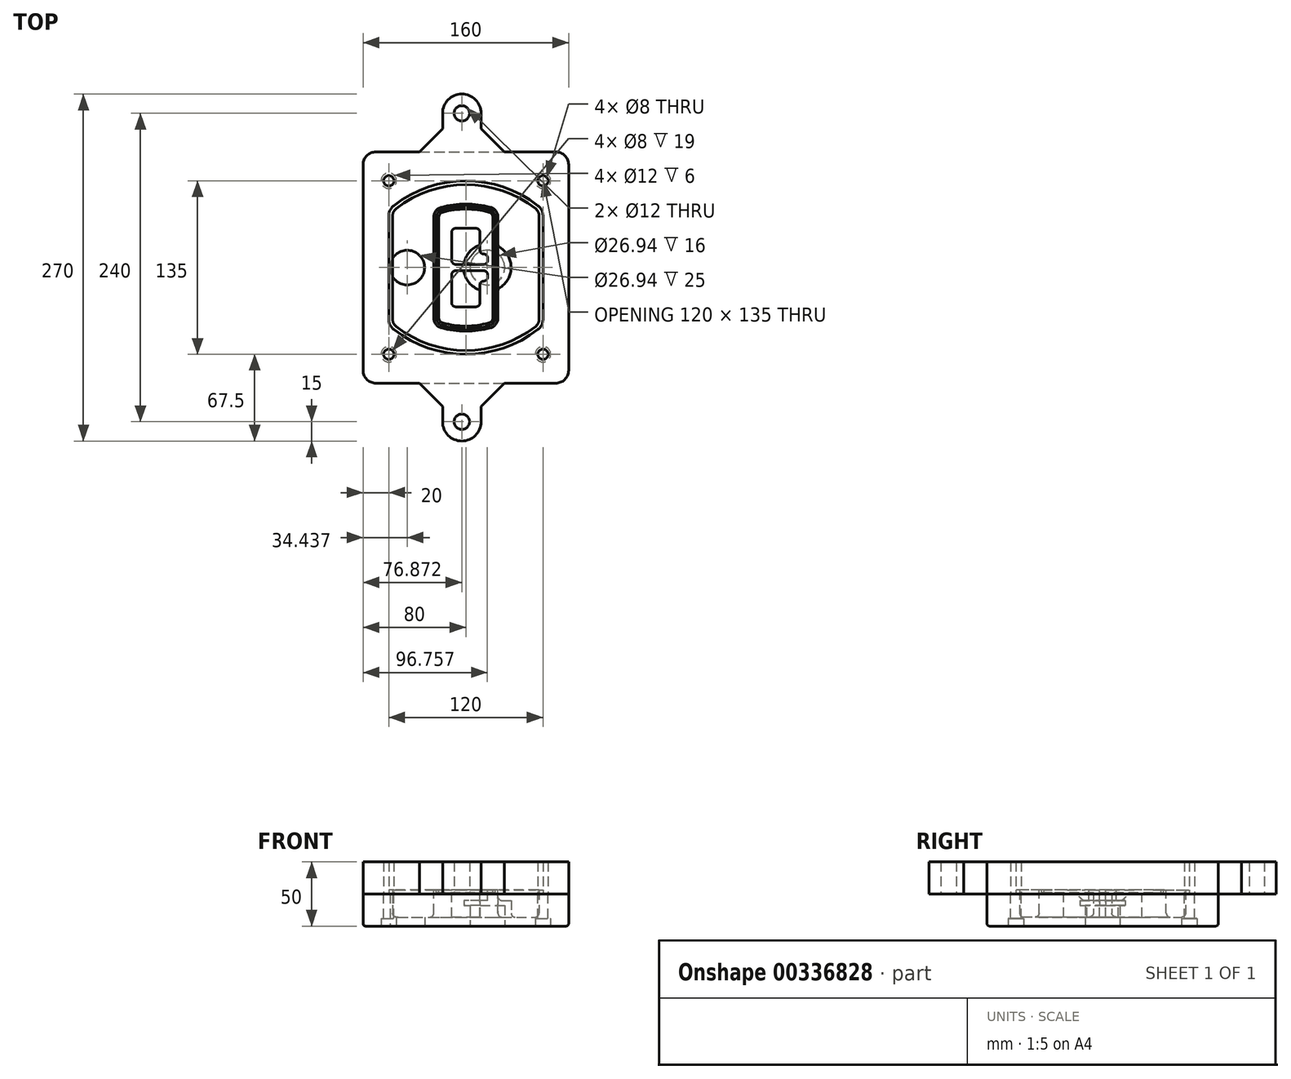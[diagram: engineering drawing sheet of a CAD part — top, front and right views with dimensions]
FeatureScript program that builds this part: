
annotation { "Feature Type Name" : "Feature", "Feature Type Description" : "" }
export const myFeature = defineFeature(function(context is Context, id is Id, definition is map)
    precondition{}
    {
        {
            var Q0;
            Q0=qCreatedBy(makeId("Top.planeOp"),FACE);
            var sketch = newSketch(context, id + "F0", { "sketchPlane" : qUnion([Q0])});
            skPoint(sketch, "E0.rect.middle", {"position": v(0, 0) * mm});
            skLineSegment(sketch, "E1.bottom", {"start": v(-70, -90) * mm, "end": v(70, -90) * mm});
            skLineSegment(sketch, "E1.top", {"start": v(-70, 90) * mm, "end": v(70, 90) * mm});
            skLineSegment(sketch, "E1.left", {"start": v(-80, -80) * mm, "end": v(-80, 80) * mm});
            skLineSegment(sketch, "E1.right", {"start": v(80, -80) * mm, "end": v(80, 80) * mm});
            skLineSegment(sketch, "E2", {"start": v(-80, 90) * mm, "end": v(80, -90) * mm, "construction": true});
            skLineSegment(sketch, "E3", {"start": v(80, 90) * mm, "end": v(-80, -90) * mm, "construction": true});
            skCircle(sketch, "E4", {"center": v(-60, 67.5) * mm, "radius": 4 * mm});
            skCircle(sketch, "E5", {"center": v(60, 67.5) * mm, "radius": 4 * mm});
            skCircle(sketch, "E6", {"center": v(60, -67.5) * mm, "radius": 4 * mm});
            skCircle(sketch, "E7", {"center": v(-60, -67.5) * mm, "radius": 4 * mm});
            skLineSegment(sketch, "E8", {"start": v(-60, 67.5) * mm, "end": v(60, 67.5) * mm, "construction": true});
            skLineSegment(sketch, "E9", {"start": v(60, 67.5) * mm, "end": v(60, -67.5) * mm, "construction": true});
            skLineSegment(sketch, "E10", {"start": v(60, -67.5) * mm, "end": v(-60, -67.5) * mm, "construction": true});
            skLineSegment(sketch, "E11", {"start": v(-60, -67.5) * mm, "end": v(-60, 67.5) * mm, "construction": true});
            skLineSegment(sketch, "E12", {"start": v(-60, 40.3) * mm, "end": v(-60, -40.3) * mm});
            skLineSegment(sketch, "E13", {"start": v(60, 40.3) * mm, "end": v(60, -40.3) * mm});
            skArc(sketch, "E14", {"start": v(56.15, 48.18) * mm, "mid": v(0, 67.5) * mm, "end": v(-56.15, 48.18) * mm});
            skArc(sketch, "E15", {"start": v(-56.15, -48.18) * mm, "mid": v(0, -67.5) * mm, "end": v(56.15, -48.18) * mm});
            skLineSegment(sketch, "E16", {"start": v(-60, 0) * mm, "end": v(60, 0) * mm, "construction": true});
            skPoint(sketch, "E17.visualSharp", {"position": v(-60, -45) * mm});
            skArc(sketch, "E17.filletArc", {"start": v(-60, -40.3) * mm, "mid": v(-58.99, -44.68) * mm, "end": v(-56.15, -48.18) * mm});
            skPoint(sketch, "E18.visualSharp", {"position": v(-60, 45) * mm});
            skArc(sketch, "E18.filletArc", {"start": v(-56.15, 48.18) * mm, "mid": v(-58.99, 44.68) * mm, "end": v(-60, 40.3) * mm});
            skPoint(sketch, "E19.visualSharp", {"position": v(60, 45) * mm});
            skArc(sketch, "E19.filletArc", {"start": v(60, 40.3) * mm, "mid": v(58.99, 44.68) * mm, "end": v(56.15, 48.18) * mm});
            skPoint(sketch, "E20.visualSharp", {"position": v(60, -45) * mm});
            skArc(sketch, "E20.filletArc", {"start": v(56.15, -48.18) * mm, "mid": v(58.99, -44.68) * mm, "end": v(60, -40.3) * mm});
            skPoint(sketch, "E21.visualSharp", {"position": v(-80, 90) * mm});
            skArc(sketch, "E21.filletArc", {"start": v(-70, 90) * mm, "mid": v(-77.07, 87.07) * mm, "end": v(-80, 80) * mm});
            skPoint(sketch, "E22.visualSharp", {"position": v(80, 90) * mm});
            skArc(sketch, "E22.filletArc", {"start": v(80, 80) * mm, "mid": v(77.07, 87.07) * mm, "end": v(70, 90) * mm});
            skPoint(sketch, "E23.visualSharp", {"position": v(80, -90) * mm});
            skArc(sketch, "E23.filletArc", {"start": v(70, -90) * mm, "mid": v(77.07, -87.07) * mm, "end": v(80, -80) * mm});
            skPoint(sketch, "E24.visualSharp", {"position": v(-80, -90) * mm});
            skArc(sketch, "E24.filletArc", {"start": v(-80, -80) * mm, "mid": v(-77.07, -87.07) * mm, "end": v(-70, -90) * mm});
            skArc(sketch, "E25.0", {"start": v(57, 40.3) * mm, "mid": v(56.3, 43.36) * mm, "end": v(54.3, 45.81) * mm});
            skLineSegment(sketch, "E25.1", {"start": v(57, 40.3) * mm, "end": v(57, -40.3) * mm});
            skArc(sketch, "E25.2", {"start": v(54.3, -45.81) * mm, "mid": v(56.3, -43.36) * mm, "end": v(57, -40.3) * mm});
            skArc(sketch, "E25.3", {"start": v(-54.3, -45.81) * mm, "mid": v(0, -64.5) * mm, "end": v(54.3, -45.81) * mm});
            skArc(sketch, "E25.4", {"start": v(-57, -40.3) * mm, "mid": v(-56.3, -43.36) * mm, "end": v(-54.3, -45.81) * mm});
            skArc(sketch, "E25.5", {"start": v(54.3, 45.81) * mm, "mid": v(0, 64.5) * mm, "end": v(-54.3, 45.81) * mm});
            skLineSegment(sketch, "E25.6", {"start": v(-57, 40.3) * mm, "end": v(-57, -40.3) * mm});
            skArc(sketch, "E25.7", {"start": v(-54.3, 45.81) * mm, "mid": v(-56.3, 43.36) * mm, "end": v(-57, 40.3) * mm});
            skArc(sketch, "E26.0", {"start": v(-58.62, 51.33) * mm, "mid": v(-62.58, 46.43) * mm, "end": v(-64, 40.3) * mm});
            skArc(sketch, "E26.1", {"start": v(58.62, 51.33) * mm, "mid": v(0, 71.5) * mm, "end": v(-58.62, 51.33) * mm});
            skArc(sketch, "E26.2", {"start": v(64, 40.3) * mm, "mid": v(62.58, 46.43) * mm, "end": v(58.62, 51.33) * mm});
            skLineSegment(sketch, "E26.3", {"start": v(64, 40.3) * mm, "end": v(64, -40.3) * mm});
            skArc(sketch, "E26.4", {"start": v(58.62, -51.33) * mm, "mid": v(62.58, -46.43) * mm, "end": v(64, -40.3) * mm});
            skLineSegment(sketch, "E26.5", {"start": v(-64, 40.3) * mm, "end": v(-64, -40.3) * mm});
            skArc(sketch, "E26.6", {"start": v(-58.62, -51.33) * mm, "mid": v(0, -71.5) * mm, "end": v(58.62, -51.33) * mm});
            skArc(sketch, "E26.7", {"start": v(-64, -40.3) * mm, "mid": v(-62.58, -46.43) * mm, "end": v(-58.62, -51.33) * mm});
            skSolve(sketch);
        }
        {
            var Q0;
            Q0=makeQuery(id+"F0.imprint","IMPRINT",FACE,{"disambiguationData":[TD([[makeQuery(id+"F0.imprint","IMPRINT",EDGE,{"derivedFrom":sQuery(id+"F0.wireOp",EDGE,"E1.bottom")}),1.0]])]});
            var Q1;
            Q1=makeQuery(id+"F0.imprint","IMPRINT",FACE,{"disambiguationData":[TD([[makeQuery(id+"F0.imprint","IMPRINT",EDGE,{"derivedFrom":sQuery(id+"F0.wireOp",EDGE,"E12")}),1.0]])]});
            var Q2;
            Q2=makeQuery(id+"F0.imprint","IMPRINT",FACE,{"disambiguationData":[TD([[makeQuery(id+"F0.imprint","IMPRINT",EDGE,{"derivedFrom":sQuery(id+"F0.wireOp",EDGE,"E25.0")}),1.0]])]});
            var Q3;
            Q3=makeQuery(id+"F0.imprint","IMPRINT",FACE,{"disambiguationData":[TD([[makeQuery(id+"F0.imprint","IMPRINT",EDGE,{"derivedFrom":sQuery(id+"F0.wireOp",EDGE,"E12")}),-1.0]])]});
            extrude(context, id + "F1", {"entities" : qUnion([Q0, Q1, Q2, Q3]), "oppositeDirection" : true, "depth" : 25 * mm});
        }
        {
            var Q0;
            Q0=makeQuery(id+"F0.imprint","IMPRINT",FACE,{"disambiguationData":[TD([[makeQuery(id+"F0.imprint","IMPRINT",EDGE,{"derivedFrom":sQuery(id+"F0.wireOp",EDGE,"E12")}),1.0]])]});
            extrude(context, id + "F2", {"entities" : qUnion([Q0]), "operationType" : NewBodyOperationType.ADD, "depth" : 3 * mm});
        }
        {
            var Q0;
            Q0=makeQuery(id+"F0.imprint","IMPRINT",FACE,{"disambiguationData":[TD([[makeQuery(id+"F0.imprint","IMPRINT",EDGE,{"derivedFrom":sQuery(id+"F0.wireOp",EDGE,"E25.0")}),1.0]])]});
            extrude(context, id + "F3", {"entities" : qUnion([Q0]), "operationType" : NewBodyOperationType.REMOVE, "oppositeDirection" : true, "depth" : 18 * mm});
        }
        {
            var Q0;
            Q0=makeQuery(id+"F2.opExtrude","CAP_FACE",FACE,{"disambiguationData":[OSD([sQuery(id+"F0.wireOp",EDGE,"E12"),sQuery(id+"F0.wireOp",EDGE,"E13"),sQuery(id+"F0.wireOp",EDGE,"E14"),sQuery(id+"F0.wireOp",EDGE,"E15"),sQuery(id+"F0.wireOp",EDGE,"E17.filletArc"),sQuery(id+"F0.wireOp",EDGE,"E18.filletArc"),sQuery(id+"F0.wireOp",EDGE,"E19.filletArc"),sQuery(id+"F0.wireOp",EDGE,"E20.filletArc"),sQuery(id+"F0.wireOp",EDGE,"E25.0"),sQuery(id+"F0.wireOp",EDGE,"E25.1"),sQuery(id+"F0.wireOp",EDGE,"E25.2"),sQuery(id+"F0.wireOp",EDGE,"E25.3"),sQuery(id+"F0.wireOp",EDGE,"E25.4"),sQuery(id+"F0.wireOp",EDGE,"E25.5"),sQuery(id+"F0.wireOp",EDGE,"E25.6"),sQuery(id+"F0.wireOp",EDGE,"E25.7")])],"isStart":false});
            var sketch = newSketch(context, id + "F4", { "sketchPlane" : qUnion([Q0])});
            skArc(sketch, "E27.0", {"start": v(-19.08, -46.97) * mm, "mid": v(0, -49.5) * mm, "end": v(19.08, -46.97) * mm});
            skArc(sketch, "E28.0", {"start": v(19.08, 46.97) * mm, "mid": v(0, 49.5) * mm, "end": v(-19.08, 46.97) * mm});
            skLineSegment(sketch, "E29", {"start": v(-25, 39.25) * mm, "end": v(-25, -39.25) * mm});
            skLineSegment(sketch, "E30", {"start": v(25, 39.25) * mm, "end": v(25, -39.25) * mm});
            skLineSegment(sketch, "E31", {"start": v(-25, 45.1) * mm, "end": v(25, 45.1) * mm, "construction": true});
            skLineSegment(sketch, "E32", {"start": v(-25, -45.1) * mm, "end": v(25, -45.1) * mm, "construction": true});
            skPoint(sketch, "E33.visualSharp", {"position": v(-25, 45.1) * mm});
            skArc(sketch, "E33.filletArc", {"start": v(-19.08, 46.97) * mm, "mid": v(-23.35, 44.11) * mm, "end": v(-25, 39.25) * mm});
            skPoint(sketch, "E34.visualSharp", {"position": v(25, 45.1) * mm});
            skArc(sketch, "E34.filletArc", {"start": v(25, 39.25) * mm, "mid": v(23.35, 44.11) * mm, "end": v(19.08, 46.97) * mm});
            skPoint(sketch, "E35.visualSharp", {"position": v(25, -45.1) * mm});
            skArc(sketch, "E35.filletArc", {"start": v(19.08, -46.97) * mm, "mid": v(23.35, -44.11) * mm, "end": v(25, -39.25) * mm});
            skPoint(sketch, "E36.visualSharp", {"position": v(-25, -45.1) * mm});
            skArc(sketch, "E36.filletArc", {"start": v(-25, -39.25) * mm, "mid": v(-23.35, -44.11) * mm, "end": v(-19.08, -46.97) * mm});
            skArc(sketch, "E37.0", {"start": v(54.3, 45.81) * mm, "mid": v(0, 64.5) * mm, "end": v(-54.3, 45.81) * mm});
            skArc(sketch, "E37.1", {"start": v(-54.3, 45.81) * mm, "mid": v(-56.3, 43.36) * mm, "end": v(-57, 40.3) * mm});
            skLineSegment(sketch, "E37.2", {"start": v(-57, 40.3) * mm, "end": v(-57, -40.3) * mm});
            skArc(sketch, "E37.3", {"start": v(-57, -40.3) * mm, "mid": v(-56.3, -43.36) * mm, "end": v(-54.3, -45.81) * mm});
            skArc(sketch, "E37.4", {"start": v(-54.3, -45.81) * mm, "mid": v(0, -64.5) * mm, "end": v(54.3, -45.81) * mm});
            skArc(sketch, "E37.5", {"start": v(54.3, -45.81) * mm, "mid": v(56.3, -43.36) * mm, "end": v(57, -40.3) * mm});
            skLineSegment(sketch, "E37.6", {"start": v(57, 40.3) * mm, "end": v(57, -40.3) * mm});
            skArc(sketch, "E37.7", {"start": v(57, 40.3) * mm, "mid": v(56.3, 43.36) * mm, "end": v(54.3, 45.81) * mm});
            skLineSegment(sketch, "E38.0", {"start": v(23, 39.25) * mm, "end": v(23, -39.25) * mm});
            skArc(sketch, "E38.1", {"start": v(18.56, -45.04) * mm, "mid": v(21.76, -42.9) * mm, "end": v(23, -39.25) * mm});
            skArc(sketch, "E38.2", {"start": v(-18.56, -45.04) * mm, "mid": v(0, -47.5) * mm, "end": v(18.56, -45.04) * mm});
            skArc(sketch, "E38.3", {"start": v(-23, -39.25) * mm, "mid": v(-21.76, -42.9) * mm, "end": v(-18.56, -45.04) * mm});
            skLineSegment(sketch, "E38.4", {"start": v(-23, 39.25) * mm, "end": v(-23, -39.25) * mm});
            skArc(sketch, "E38.5", {"start": v(23, 39.25) * mm, "mid": v(21.76, 42.9) * mm, "end": v(18.56, 45.04) * mm});
            skArc(sketch, "E38.6", {"start": v(-18.56, 45.04) * mm, "mid": v(-21.76, 42.9) * mm, "end": v(-23, 39.25) * mm});
            skArc(sketch, "E38.7", {"start": v(18.56, 45.04) * mm, "mid": v(0, 47.5) * mm, "end": v(-18.56, 45.04) * mm});
            skArc(sketch, "E39.0", {"start": v(21, 39.25) * mm, "mid": v(20.18, 41.68) * mm, "end": v(18.04, 43.1) * mm});
            skLineSegment(sketch, "E39.1", {"start": v(21, 39.25) * mm, "end": v(21, -39.25) * mm});
            skArc(sketch, "E39.2", {"start": v(18.04, -43.1) * mm, "mid": v(20.18, -41.68) * mm, "end": v(21, -39.25) * mm});
            skArc(sketch, "E39.3", {"start": v(-18.04, -43.1) * mm, "mid": v(0, -45.5) * mm, "end": v(18.04, -43.1) * mm});
            skArc(sketch, "E39.4", {"start": v(-21, -39.25) * mm, "mid": v(-20.18, -41.68) * mm, "end": v(-18.04, -43.1) * mm});
            skArc(sketch, "E39.5", {"start": v(18.04, 43.1) * mm, "mid": v(0, 45.5) * mm, "end": v(-18.04, 43.1) * mm});
            skLineSegment(sketch, "E39.6", {"start": v(-21, 39.25) * mm, "end": v(-21, -39.25) * mm});
            skArc(sketch, "E39.7", {"start": v(-18.04, 43.1) * mm, "mid": v(-20.18, 41.68) * mm, "end": v(-21, 39.25) * mm});
            skLineSegment(sketch, "E40", {"start": v(-25, 0) * mm, "end": v(25, 0) * mm, "construction": true});
            skLineSegment(sketch, "E41", {"start": v(-11, 5.5) * mm, "end": v(-11, 27.5) * mm});
            skLineSegment(sketch, "E42", {"start": v(-8, 30.5) * mm, "end": v(8, 30.5) * mm});
            skLineSegment(sketch, "E43", {"start": v(11, 27.5) * mm, "end": v(11, 13.5) * mm});
            skLineSegment(sketch, "E44", {"start": v(14, 10.5) * mm, "end": v(14, 10.5) * mm});
            skLineSegment(sketch, "E45", {"start": v(17, 7.5) * mm, "end": v(17, 5.5) * mm});
            skLineSegment(sketch, "E46", {"start": v(14, 2.5) * mm, "end": v(-8, 2.5) * mm});
            skPoint(sketch, "E47.visualSharp", {"position": v(-11, 30.5) * mm});
            skArc(sketch, "E47.filletArc", {"start": v(-8, 30.5) * mm, "mid": v(-10.12, 29.62) * mm, "end": v(-11, 27.5) * mm});
            skPoint(sketch, "E48.visualSharp", {"position": v(11, 30.5) * mm});
            skArc(sketch, "E48.filletArc", {"start": v(11, 27.5) * mm, "mid": v(10.12, 29.62) * mm, "end": v(8, 30.5) * mm});
            skPoint(sketch, "E49.visualSharp", {"position": v(11, 10.5) * mm});
            skArc(sketch, "E49.filletArc", {"start": v(11, 13.5) * mm, "mid": v(11.88, 11.38) * mm, "end": v(14, 10.5) * mm});
            skPoint(sketch, "E50.visualSharp", {"position": v(17, 10.5) * mm});
            skArc(sketch, "E50.filletArc", {"start": v(17, 7.5) * mm, "mid": v(16.12, 9.62) * mm, "end": v(14, 10.5) * mm});
            skPoint(sketch, "E51.visualSharp", {"position": v(17, 2.5) * mm});
            skArc(sketch, "E51.filletArc", {"start": v(14, 2.5) * mm, "mid": v(16.12, 3.38) * mm, "end": v(17, 5.5) * mm});
            skPoint(sketch, "E52.visualSharp", {"position": v(-11, 2.5) * mm});
            skArc(sketch, "E52.filletArc", {"start": v(-11, 5.5) * mm, "mid": v(-10.12, 3.38) * mm, "end": v(-8, 2.5) * mm});
            skLineSegment(sketch, "E53.0.MirrorCS", {"start": v(14, -2.5) * mm, "end": v(-8, -2.5) * mm});
            skArc(sketch, "E54.0.MirrorCS", {"start": v(-11, -5.5) * mm, "mid": v(-10.12, -3.38) * mm, "end": v(-8, -2.5) * mm});
            skLineSegment(sketch, "E55.0.MirrorCS", {"start": v(-11, -5.5) * mm, "end": v(-11, -27.5) * mm});
            skArc(sketch, "E56.0.MirrorCS", {"start": v(-8, -30.5) * mm, "mid": v(-10.12, -29.62) * mm, "end": v(-11, -27.5) * mm});
            skLineSegment(sketch, "E57.0.MirrorCS", {"start": v(-8, -30.5) * mm, "end": v(8, -30.5) * mm});
            skArc(sketch, "E58.0.MirrorCS", {"start": v(11, -27.5) * mm, "mid": v(10.12, -29.62) * mm, "end": v(8, -30.5) * mm});
            skLineSegment(sketch, "E59.0.MirrorCS", {"start": v(11, -27.5) * mm, "end": v(11, -13.5) * mm});
            skArc(sketch, "E60.0.MirrorCS", {"start": v(11, -13.5) * mm, "mid": v(11.88, -11.38) * mm, "end": v(14, -10.5) * mm});
            skArc(sketch, "E61.0.MirrorCS", {"start": v(17, -7.5) * mm, "mid": v(16.12, -9.62) * mm, "end": v(14, -10.5) * mm});
            skLineSegment(sketch, "E62.0.MirrorCS", {"start": v(17, -7.5) * mm, "end": v(17, -5.5) * mm});
            skArc(sketch, "E63.0.MirrorCS", {"start": v(14, -2.5) * mm, "mid": v(16.12, -3.38) * mm, "end": v(17, -5.5) * mm});
            skSolve(sketch);
        }
        {
            var Q0;
            Q0=makeQuery(id+"F4.imprint","IMPRINT",FACE,{"disambiguationData":[TD([[makeQuery(id+"F4.imprint","IMPRINT",EDGE,{"derivedFrom":sQuery(id+"F4.wireOp",EDGE,"E27.0")}),1.0]])]});
            var Q1;
            Q1=makeQuery(id+"F4.imprint","IMPRINT",FACE,{"disambiguationData":[TD([[makeQuery(id+"F4.imprint","IMPRINT",EDGE,{"derivedFrom":sQuery(id+"F4.wireOp",EDGE,"E38.0")}),-1.0]])]});
            var Q2;
            Q2=makeQuery(id+"F4.imprint","IMPRINT",FACE,{"disambiguationData":[TD([[makeQuery(id+"F4.imprint","IMPRINT",EDGE,{"derivedFrom":sQuery(id+"F4.wireOp",EDGE,"E39.0")}),1.0]])]});
            extrude(context, id + "F5", {"entities" : qUnion([Q0, Q1, Q2]), "operationType" : NewBodyOperationType.ADD, "endBound" : BoundingType.UP_TO_NEXT, "oppositeDirection" : true, "depth" : 25 * mm});
        }
        {
            var Q0;
            Q0=makeQuery(id+"F4.imprint","IMPRINT",FACE,{"disambiguationData":[TD([[makeQuery(id+"F4.imprint","IMPRINT",EDGE,{"derivedFrom":sQuery(id+"F4.wireOp",EDGE,"E38.0")}),-1.0]])]});
            extrude(context, id + "F6", {"entities" : qUnion([Q0]), "operationType" : NewBodyOperationType.REMOVE, "oppositeDirection" : true, "depth" : 2 * mm});
        }
        {
            var Q0;
            Q0=makeQuery(id+"F1.opExtrude","CAP_FACE",FACE,{"disambiguationData":[OSD([sQuery(id+"F0.wireOp",EDGE,"E1.bottom"),sQuery(id+"F0.wireOp",EDGE,"E1.top"),sQuery(id+"F0.wireOp",EDGE,"E1.left"),sQuery(id+"F0.wireOp",EDGE,"E1.right"),sQuery(id+"F0.wireOp",EDGE,"E4"),sQuery(id+"F0.wireOp",EDGE,"E5"),sQuery(id+"F0.wireOp",EDGE,"E6"),sQuery(id+"F0.wireOp",EDGE,"E7"),sQuery(id+"F0.wireOp",EDGE,"E21.filletArc"),sQuery(id+"F0.wireOp",EDGE,"E22.filletArc"),sQuery(id+"F0.wireOp",EDGE,"E23.filletArc"),sQuery(id+"F0.wireOp",EDGE,"E24.filletArc")])],"isStart":false});
            var sketch = newSketch(context, id + "F7", { "sketchPlane" : qUnion([Q0])});
            skCircle(sketch, "E64", {"center": v(16.76, 0) * mm, "radius": 13.47 * mm});
            skCircle(sketch, "E65", {"center": v(-45.56, 0) * mm, "radius": 13.47 * mm});
            skLineSegment(sketch, "E66", {"start": v(80, 0) * mm, "end": v(-80, 0) * mm});
            skCircle(sketch, "E67", {"center": v(16.76, 0) * mm, "radius": 18.47 * mm});
            skCircle(sketch, "E68", {"center": v(60, -67.5) * mm, "radius": 6 * mm});
            skCircle(sketch, "E69", {"center": v(-60, -67.5) * mm, "radius": 6 * mm});
            skCircle(sketch, "E70", {"center": v(-60, 67.5) * mm, "radius": 6 * mm});
            skCircle(sketch, "E71", {"center": v(60, 67.5) * mm, "radius": 6 * mm});
            skSolve(sketch);
        }
        {
            var Q0;
            {var subQ1=sQuery(id+"F7.wireOp",EDGE,"E66");var subQ4=sQuery(id+"F7.wireOp",EDGE,"E64");var subQ6=makeQuery(id+"F7.imprint","INTERSECT",VERTEX,{"disambiguationData":[OD(0.0)],"derivedFrom":[subQ4,subQ1]});Q0=makeQuery(id+"F7.imprint","IMPRINT",FACE,{"disambiguationData":[TD([[makeQuery(id+"F7.imprint","IMPRINT",EDGE,{"disambiguationData":[TD([[subQ6,-1.0]])],"derivedFrom":subQ4}),-1.0]])]});}
            var Q1;
            {var subQ0=sQuery(id+"F7.wireOp",EDGE,"E66");var subQ1=sQuery(id+"F7.wireOp",EDGE,"E64");var subQ3=makeQuery(id+"F7.imprint","INTERSECT",VERTEX,{"disambiguationData":[OD(0.0)],"derivedFrom":[subQ1,subQ0]});Q1=makeQuery(id+"F7.imprint","IMPRINT",FACE,{"disambiguationData":[TD([[makeQuery(id+"F7.imprint","IMPRINT",EDGE,{"disambiguationData":[TD([[subQ3,-1.0]])],"derivedFrom":subQ1}),1.0]])]});}
            var Q2;
            {var subQ0=sQuery(id+"F7.wireOp",EDGE,"E66");var subQ1=sQuery(id+"F7.wireOp",EDGE,"E64");var subQ3=makeQuery(id+"F7.imprint","INTERSECT",VERTEX,{"disambiguationData":[OD(0.0)],"derivedFrom":[subQ1,subQ0]});Q2=makeQuery(id+"F7.imprint","IMPRINT",FACE,{"disambiguationData":[TD([[makeQuery(id+"F7.imprint","IMPRINT",EDGE,{"disambiguationData":[TD([[subQ3,1.0]])],"derivedFrom":subQ1}),1.0]])]});}
            var Q3;
            {var subQ1=sQuery(id+"F7.wireOp",EDGE,"E66");var subQ4=sQuery(id+"F7.wireOp",EDGE,"E64");var subQ6=makeQuery(id+"F7.imprint","INTERSECT",VERTEX,{"disambiguationData":[OD(0.0)],"derivedFrom":[subQ4,subQ1]});Q3=makeQuery(id+"F7.imprint","IMPRINT",FACE,{"disambiguationData":[TD([[makeQuery(id+"F7.imprint","IMPRINT",EDGE,{"disambiguationData":[TD([[subQ6,1.0]])],"derivedFrom":subQ4}),-1.0]])]});}
            extrude(context, id + "F8", {"entities" : qUnion([Q0, Q1, Q2, Q3]), "operationType" : NewBodyOperationType.ADD, "oppositeDirection" : true, "depth" : 20 * mm});
        }
        {
            var Q0;
            {var subQ0=sQuery(id+"F7.wireOp",EDGE,"E66");var subQ1=sQuery(id+"F7.wireOp",EDGE,"E64");var subQ3=makeQuery(id+"F7.imprint","INTERSECT",VERTEX,{"disambiguationData":[OD(0.0)],"derivedFrom":[subQ1,subQ0]});Q0=makeQuery(id+"F7.imprint","IMPRINT",FACE,{"disambiguationData":[TD([[makeQuery(id+"F7.imprint","IMPRINT",EDGE,{"disambiguationData":[TD([[subQ3,-1.0]])],"derivedFrom":subQ1}),1.0]])]});}
            var Q1;
            {var subQ0=sQuery(id+"F7.wireOp",EDGE,"E66");var subQ1=sQuery(id+"F7.wireOp",EDGE,"E64");var subQ3=makeQuery(id+"F7.imprint","INTERSECT",VERTEX,{"disambiguationData":[OD(0.0)],"derivedFrom":[subQ1,subQ0]});Q1=makeQuery(id+"F7.imprint","IMPRINT",FACE,{"disambiguationData":[TD([[makeQuery(id+"F7.imprint","IMPRINT",EDGE,{"disambiguationData":[TD([[subQ3,1.0]])],"derivedFrom":subQ1}),1.0]])]});}
            extrude(context, id + "F9", {"entities" : qUnion([Q0, Q1]), "operationType" : NewBodyOperationType.REMOVE, "oppositeDirection" : true, "depth" : 16 * mm});
        }
        {
            var Q0;
            {var subQ0=sQuery(id+"F7.wireOp",EDGE,"E66");var subQ1=sQuery(id+"F7.wireOp",EDGE,"E65");var subQ3=makeQuery(id+"F7.imprint","INTERSECT",VERTEX,{"disambiguationData":[OD(0.0)],"derivedFrom":[subQ1,subQ0]});Q0=makeQuery(id+"F7.imprint","IMPRINT",FACE,{"disambiguationData":[TD([[makeQuery(id+"F7.imprint","IMPRINT",EDGE,{"disambiguationData":[TD([[subQ3,-1.0]])],"derivedFrom":subQ1}),1.0]])]});}
            var Q1;
            {var subQ0=sQuery(id+"F7.wireOp",EDGE,"E66");var subQ1=sQuery(id+"F7.wireOp",EDGE,"E65");var subQ3=makeQuery(id+"F7.imprint","INTERSECT",VERTEX,{"disambiguationData":[OD(0.0)],"derivedFrom":[subQ1,subQ0]});Q1=makeQuery(id+"F7.imprint","IMPRINT",FACE,{"disambiguationData":[TD([[makeQuery(id+"F7.imprint","IMPRINT",EDGE,{"disambiguationData":[TD([[subQ3,1.0]])],"derivedFrom":subQ1}),1.0]])]});}
            extrude(context, id + "F10", {"entities" : qUnion([Q0, Q1]), "operationType" : NewBodyOperationType.REMOVE, "oppositeDirection" : true, "depth" : 25 * mm});
        }
        {
            var Q0;
            Q0=makeQuery(id+"F7.imprint","IMPRINT",FACE,{"disambiguationData":[TD([[makeQuery(id+"F7.imprint","IMPRINT",EDGE,{"derivedFrom":sQuery(id+"F7.wireOp",EDGE,"E68")}),1.0]])]});
            var Q1;
            Q1=makeQuery(id+"F7.imprint","IMPRINT",FACE,{"disambiguationData":[TD([[makeQuery(id+"F7.imprint","IMPRINT",EDGE,{"derivedFrom":makeQuery(id+"F1.opExtrude","CAP_EDGE",EDGE,{"disambiguationData":[OSD([sQuery(id+"F0.wireOp",EDGE,"E5")])],"isStart":false})}),-1.0]])]});
            var Q2;
            Q2=makeQuery(id+"F7.imprint","IMPRINT",FACE,{"disambiguationData":[TD([[makeQuery(id+"F7.imprint","IMPRINT",EDGE,{"derivedFrom":sQuery(id+"F7.wireOp",EDGE,"E69")}),1.0]])]});
            var Q3;
            Q3=makeQuery(id+"F7.imprint","IMPRINT",FACE,{"disambiguationData":[TD([[makeQuery(id+"F7.imprint","IMPRINT",EDGE,{"derivedFrom":makeQuery(id+"F1.opExtrude","CAP_EDGE",EDGE,{"disambiguationData":[OSD([sQuery(id+"F0.wireOp",EDGE,"E4")])],"isStart":false})}),-1.0]])]});
            var Q4;
            Q4=makeQuery(id+"F7.imprint","IMPRINT",FACE,{"disambiguationData":[TD([[makeQuery(id+"F7.imprint","IMPRINT",EDGE,{"derivedFrom":sQuery(id+"F7.wireOp",EDGE,"E70")}),1.0]])]});
            var Q5;
            Q5=makeQuery(id+"F7.imprint","IMPRINT",FACE,{"disambiguationData":[TD([[makeQuery(id+"F7.imprint","IMPRINT",EDGE,{"derivedFrom":makeQuery(id+"F1.opExtrude","CAP_EDGE",EDGE,{"disambiguationData":[OSD([sQuery(id+"F0.wireOp",EDGE,"E7")])],"isStart":false})}),-1.0]])]});
            var Q6;
            Q6=makeQuery(id+"F7.imprint","IMPRINT",FACE,{"disambiguationData":[TD([[makeQuery(id+"F7.imprint","IMPRINT",EDGE,{"derivedFrom":sQuery(id+"F7.wireOp",EDGE,"E71")}),1.0]])]});
            var Q7;
            Q7=makeQuery(id+"F7.imprint","IMPRINT",FACE,{"disambiguationData":[TD([[makeQuery(id+"F7.imprint","IMPRINT",EDGE,{"derivedFrom":makeQuery(id+"F1.opExtrude","CAP_EDGE",EDGE,{"disambiguationData":[OSD([sQuery(id+"F0.wireOp",EDGE,"E6")])],"isStart":false})}),-1.0]])]});
            extrude(context, id + "F11", {"entities" : qUnion([Q0, Q1, Q2, Q3, Q4, Q5, Q6, Q7]), "operationType" : NewBodyOperationType.REMOVE, "oppositeDirection" : true, "depth" : 6 * mm});
        }
        {
            var Q0;
            Q0=makeQuery(id+"F9.boolean.opBoolean","COPY",FACE,{"derivedFrom":makeQuery(id+"F9.opExtrude","CAP_FACE",FACE,{"disambiguationData":[OSD([sQuery(id+"F7.wireOp",EDGE,"E64")])],"isStart":false})});
            var sketch = newSketch(context, id + "F12", { "sketchPlane" : qUnion([Q0])});
            skArc(sketch, "E72.0", {"start": v(11, 17.55) * mm, "mid": v(2.57, 11.82) * mm, "end": v(-1.54, 2.5) * mm});
            skArc(sketch, "E72.1", {"start": v(-1.54, -2.5) * mm, "mid": v(2.57, -11.82) * mm, "end": v(11, -17.55) * mm});
            skLineSegment(sketch, "E73", {"start": v(-1.54, -2.5) * mm, "end": v(14, -2.5) * mm});
            skLineSegment(sketch, "E74.0", {"start": v(14, 2.5) * mm, "end": v(-1.54, 2.5) * mm});
            skArc(sketch, "E74.1", {"start": v(14, 2.5) * mm, "mid": v(16.12, 3.38) * mm, "end": v(17, 5.5) * mm});
            skLineSegment(sketch, "E74.2", {"start": v(17, 7.5) * mm, "end": v(17, 5.5) * mm});
            skArc(sketch, "E74.3", {"start": v(17, 7.5) * mm, "mid": v(16.12, 9.62) * mm, "end": v(14, 10.5) * mm});
            skArc(sketch, "E74.4", {"start": v(11, 13.5) * mm, "mid": v(11.88, 11.38) * mm, "end": v(14, 10.5) * mm});
            skLineSegment(sketch, "E74.5", {"start": v(11, 17.55) * mm, "end": v(11, 13.5) * mm});
            skLineSegment(sketch, "E74.7", {"start": v(14, -2.5) * mm, "end": v(-1.54, -2.5) * mm});
            skArc(sketch, "E74.8", {"start": v(14, -2.5) * mm, "mid": v(16.12, -3.38) * mm, "end": v(17, -5.5) * mm});
            skLineSegment(sketch, "E74.9", {"start": v(17, -7.5) * mm, "end": v(17, -5.5) * mm});
            skArc(sketch, "E74.10", {"start": v(17, -7.5) * mm, "mid": v(16.12, -9.62) * mm, "end": v(14, -10.5) * mm});
            skArc(sketch, "E74.11", {"start": v(11, -13.5) * mm, "mid": v(11.88, -11.38) * mm, "end": v(14, -10.5) * mm});
            skLineSegment(sketch, "E74.12", {"start": v(11, -17.55) * mm, "end": v(11, -13.5) * mm});
            skPoint(sketch, "E75.orphan", {"position": v(11, -27.5) * mm});
            skPoint(sketch, "E76.orphan", {"position": v(-8, -2.5) * mm});
            skPoint(sketch, "E77.orphan", {"position": v(-8, 2.5) * mm});
            skPoint(sketch, "E78.orphan", {"position": v(11, 27.5) * mm});
            skSolve(sketch);
        }
        {
            var Q0;
            {var subQ7=sQuery(id+"F12.wireOp",EDGE,"E72.0");var subQ14=sQuery(id+"F12.wireOp",EDGE,"E72.1");var subQ16=sQuery(id+"F12.wireOp",EDGE,"E74.1");var subQ18=sQuery(id+"F12.wireOp",EDGE,"E74.8");Q0=qUnion([makeQuery(id+"F12.imprint","IMPRINT",FACE,{"disambiguationData":[TD([[makeQuery(id+"F12.imprint","IMPRINT",EDGE,{"derivedFrom":subQ7}),1.0]])]}),makeQuery(id+"F12.imprint","IMPRINT",FACE,{"disambiguationData":[TD([[makeQuery(id+"F12.imprint","IMPRINT",EDGE,{"derivedFrom":subQ14}),1.0]])]}),makeQuery(id+"F12.imprint","IMPRINT",FACE,{"disambiguationData":[TD([[makeQuery(id+"F12.imprint","IMPRINT",EDGE,{"derivedFrom":subQ16}),1.0]])]}),makeQuery(id+"F12.imprint","IMPRINT",FACE,{"disambiguationData":[TD([[makeQuery(id+"F12.imprint","IMPRINT",EDGE,{"derivedFrom":subQ18}),-1.0]])]})]);}
            var Q1;
            Q1=makeQuery(id+"F5.boolean.opBoolean","SPLIT",FACE,{"disambiguationData":[TD([makeQuery(id+"F5.opExtrude","SWEPT_FACE",FACE,{"disambiguationData":[OSD([sQuery(id+"F4.wireOp",EDGE,"E41")])]})])],"derivedFrom":makeQuery(id+"F3.boolean.opBoolean","COPY",FACE,{"derivedFrom":makeQuery(id+"F3.opExtrude","CAP_FACE",FACE,{"disambiguationData":[OSD([sQuery(id+"F0.wireOp",EDGE,"E25.0"),sQuery(id+"F0.wireOp",EDGE,"E25.1"),sQuery(id+"F0.wireOp",EDGE,"E25.2"),sQuery(id+"F0.wireOp",EDGE,"E25.3"),sQuery(id+"F0.wireOp",EDGE,"E25.4"),sQuery(id+"F0.wireOp",EDGE,"E25.5"),sQuery(id+"F0.wireOp",EDGE,"E25.6"),sQuery(id+"F0.wireOp",EDGE,"E25.7")])],"isStart":false})})});
            extrude(context, id + "F13", {"entities" : qUnion([Q0]), "operationType" : NewBodyOperationType.REMOVE, "endBound" : BoundingType.UP_TO_SURFACE, "endBoundEntityFace" : qUnion([Q1]), "depth" : 25 * mm});
        }
        {
            var Q0;
            Q0=makeQuery(id+"F3.boolean.opBoolean","COPY",EDGE,{"derivedFrom":makeQuery(id+"F3.opExtrude","CAP_EDGE",EDGE,{"disambiguationData":[OSD([sQuery(id+"F0.wireOp",EDGE,"E25.6")])],"isStart":false})});
            var Q1;
            Q1=makeQuery(id+"F8.boolean.opBoolean","INTERSECT",EDGE,{"derivedFrom":[makeQuery(id+"F5.opExtrude","SWEPT_FACE",FACE,{"disambiguationData":[OSD([sQuery(id+"F4.wireOp",EDGE,"E30")])]}),makeQuery(id+"F8.opExtrude","CAP_FACE",FACE,{"disambiguationData":[OSD([sQuery(id+"F7.wireOp",EDGE,"E67")])],"isStart":false})]});
            var Q2;
            Q2=makeQuery(id+"F8.boolean.opBoolean","INTERSECT",EDGE,{"disambiguationData":[OD(1.0)],"derivedFrom":[makeQuery(id+"F5.opExtrude","SWEPT_FACE",FACE,{"disambiguationData":[OSD([sQuery(id+"F4.wireOp",EDGE,"E30")])]}),makeQuery(id+"F8.opExtrude","SWEPT_FACE",FACE,{"disambiguationData":[OSD([sQuery(id+"F7.wireOp",EDGE,"E67")])]})]});
            var Q3;
            {var subQ0=sQuery(id+"F4.wireOp",EDGE,"E30");Q3=makeQuery(id+"F8.boolean.opBoolean","SPLIT",EDGE,{"disambiguationData":[TD([makeQuery(id+"F5.opExtrude","SWEPT_FACE",FACE,{"disambiguationData":[OSD([sQuery(id+"F4.wireOp",EDGE,"E35.filletArc")])]})])],"derivedFrom":makeQuery(id+"F5.opExtrude","CAP_EDGE",EDGE,{"disambiguationData":[OSD([subQ0])],"isStart":false})});}
            var Q4;
            {var subQ0=sQuery(id+"F0.wireOp",EDGE,"E25.7");var subQ1=sQuery(id+"F0.wireOp",EDGE,"E25.1");var subQ2=sQuery(id+"F0.wireOp",EDGE,"E25.6");var subQ3=sQuery(id+"F0.wireOp",EDGE,"E25.5");var subQ4=sQuery(id+"F0.wireOp",EDGE,"E25.4");var subQ5=sQuery(id+"F0.wireOp",EDGE,"E25.0");var subQ6=sQuery(id+"F0.wireOp",EDGE,"E25.2");var subQ7=sQuery(id+"F0.wireOp",EDGE,"E25.3");Q4=makeQuery(id+"F8.boolean.opBoolean","INTERSECT",EDGE,{"derivedFrom":[makeQuery(id+"F5.boolean.opBoolean","SPLIT",FACE,{"disambiguationData":[TD([makeQuery(id+"F2.opExtrude","SWEPT_FACE",FACE,{"disambiguationData":[OSD([subQ5])]})])],"derivedFrom":makeQuery(id+"F3.boolean.opBoolean","COPY",FACE,{"derivedFrom":makeQuery(id+"F3.opExtrude","CAP_FACE",FACE,{"disambiguationData":[OSD([subQ5,subQ1,subQ6,subQ7,subQ4,subQ3,subQ2,subQ0])],"isStart":false})})}),makeQuery(id+"F8.opExtrude","SWEPT_FACE",FACE,{"disambiguationData":[OSD([sQuery(id+"F7.wireOp",EDGE,"E67")])]})]});}
            var Q5;
            Q5=makeQuery(id+"F8.boolean.opBoolean","INTERSECT",EDGE,{"disambiguationData":[OD(0.0)],"derivedFrom":[makeQuery(id+"F5.opExtrude","SWEPT_FACE",FACE,{"disambiguationData":[OSD([sQuery(id+"F4.wireOp",EDGE,"E30")])]}),makeQuery(id+"F8.opExtrude","SWEPT_FACE",FACE,{"disambiguationData":[OSD([sQuery(id+"F7.wireOp",EDGE,"E67")])]})]});
            fillet(context, id + "F14", {"entities" : qUnion([Q0, Q1, Q2, Q3, Q4, Q5]), "radius" : 3 * mm, "tangentPropagation" : true, "allowEdgeOverflow" : false});
        }
        {
            var Q0;
            Q0=makeQuery(id+"F1.opExtrude","CAP_EDGE",EDGE,{"disambiguationData":[OSD([sQuery(id+"F0.wireOp",EDGE,"E1.bottom")])],"isStart":false});
            fillet(context, id + "F15", {"entities" : qUnion([Q0]), "radius" : 2 * mm, "tangentPropagation" : true, "allowEdgeOverflow" : false});
        }
        {
            var Q0;
            {var subQ0=sQuery(id+"F0.wireOp",EDGE,"E21.filletArc");var subQ1=sQuery(id+"F0.wireOp",EDGE,"E7");var subQ2=sQuery(id+"F0.wireOp",EDGE,"E6");var subQ3=sQuery(id+"F0.wireOp",EDGE,"E5");var subQ4=sQuery(id+"F0.wireOp",EDGE,"E4");var subQ5=sQuery(id+"F0.wireOp",EDGE,"E22.filletArc");var subQ6=sQuery(id+"F0.wireOp",EDGE,"E1.bottom");var subQ7=sQuery(id+"F0.wireOp",EDGE,"E1.right");var subQ8=sQuery(id+"F0.wireOp",EDGE,"E1.top");var subQ9=sQuery(id+"F0.wireOp",EDGE,"E1.left");var subQ10=sQuery(id+"F0.wireOp",EDGE,"E23.filletArc");var subQ11=sQuery(id+"F0.wireOp",EDGE,"E24.filletArc");Q0=makeQuery(id+"F2.boolean.opBoolean","SPLIT",FACE,{"disambiguationData":[TD([makeQuery(id+"F1.opExtrude","SWEPT_FACE",FACE,{"disambiguationData":[OSD([subQ6])]})])],"derivedFrom":makeQuery(id+"F1.opExtrude","CAP_FACE",FACE,{"disambiguationData":[OSD([subQ6,subQ8,subQ9,subQ7,subQ4,subQ3,subQ2,subQ1,subQ0,subQ5,subQ10,subQ11])],"isStart":true})});}
            var sketch = newSketch(context, id + "F16", { "sketchPlane" : qUnion([Q0])});
            skCircle(sketch, "E79.0", {"center": v(-60, 67.5) * mm, "radius": 4 * mm});
            skArc(sketch, "E79.1", {"start": v(56.15, 48.18) * mm, "mid": v(0, 67.5) * mm, "end": v(-56.15, 48.18) * mm});
            skArc(sketch, "E79.2", {"start": v(60, 40.3) * mm, "mid": v(58.99, 44.68) * mm, "end": v(56.15, 48.18) * mm});
            skLineSegment(sketch, "E79.3", {"start": v(60, 40.3) * mm, "end": v(60, -40.3) * mm});
            skLineSegment(sketch, "E79.4", {"start": v(80, -80) * mm, "end": v(80, 80) * mm});
            skArc(sketch, "E79.5", {"start": v(80, 80) * mm, "mid": v(77.07, 87.07) * mm, "end": v(70, 90) * mm});
            skLineSegment(sketch, "E79.6", {"start": v(-70, 90) * mm, "end": v(70, 90) * mm});
            skArc(sketch, "E79.7", {"start": v(-70, 90) * mm, "mid": v(-77.07, 87.07) * mm, "end": v(-80, 80) * mm});
            skLineSegment(sketch, "E79.8", {"start": v(-80, -80) * mm, "end": v(-80, 80) * mm});
            skLineSegment(sketch, "E79.9", {"start": v(-60, 40.3) * mm, "end": v(-60, -40.3) * mm});
            skArc(sketch, "E79.10", {"start": v(-56.15, 48.18) * mm, "mid": v(-58.99, 44.68) * mm, "end": v(-60, 40.3) * mm});
            skArc(sketch, "E79.11", {"start": v(-60, -40.3) * mm, "mid": v(-58.99, -44.68) * mm, "end": v(-56.15, -48.18) * mm});
            skCircle(sketch, "E79.12", {"center": v(-60, -67.5) * mm, "radius": 4 * mm});
            skArc(sketch, "E79.13", {"start": v(-56.15, -48.18) * mm, "mid": v(0, -67.5) * mm, "end": v(56.15, -48.18) * mm});
            skArc(sketch, "E79.14", {"start": v(56.15, -48.18) * mm, "mid": v(58.99, -44.68) * mm, "end": v(60, -40.3) * mm});
            skCircle(sketch, "E79.15", {"center": v(60, -67.5) * mm, "radius": 4 * mm});
            skCircle(sketch, "E79.16", {"center": v(60, 67.5) * mm, "radius": 4 * mm});
            skArc(sketch, "E79.17", {"start": v(70, -90) * mm, "mid": v(77.07, -87.07) * mm, "end": v(80, -80) * mm});
            skLineSegment(sketch, "E79.18", {"start": v(-70, -90) * mm, "end": v(70, -90) * mm});
            skArc(sketch, "E79.19", {"start": v(-80, -80) * mm, "mid": v(-77.07, -87.07) * mm, "end": v(-70, -90) * mm});
            skLineSegment(sketch, "E80", {"start": v(-36.13, 90) * mm, "end": v(-18.13, 108) * mm});
            skLineSegment(sketch, "E81", {"start": v(29.87, 90) * mm, "end": v(11.87, 108) * mm});
            skLineSegment(sketch, "E82", {"start": v(-18.13, 108) * mm, "end": v(-18.13, 120) * mm});
            skLineSegment(sketch, "E83", {"start": v(11.87, 108) * mm, "end": v(11.87, 120) * mm});
            skArc(sketch, "E84", {"start": v(11.87, 120) * mm, "mid": v(-3.13, 135) * mm, "end": v(-18.13, 120) * mm});
            skCircle(sketch, "E85", {"center": v(-3.13, 120) * mm, "radius": 6 * mm});
            skLineSegment(sketch, "E86", {"start": v(-3.13, 120) * mm, "end": v(-3.13, 90) * mm, "construction": true});
            skLineSegment(sketch, "E87", {"start": v(-80, 0) * mm, "end": v(80, 0) * mm, "construction": true});
            skCircle(sketch, "E88.MirrorC", {"center": v(-3.13, -120) * mm, "radius": 6 * mm});
            skArc(sketch, "E89.MirrorCS", {"start": v(11.87, -120) * mm, "mid": v(-3.13, -135) * mm, "end": v(-18.13, -120) * mm});
            skLineSegment(sketch, "E90.MirrorCS", {"start": v(-18.13, -108) * mm, "end": v(-18.13, -120) * mm});
            skLineSegment(sketch, "E91.MirrorCS", {"start": v(11.87, -108) * mm, "end": v(11.87, -120) * mm});
            skLineSegment(sketch, "E92.MirrorCS", {"start": v(-36.13, -90) * mm, "end": v(-18.13, -108) * mm});
            skLineSegment(sketch, "E93.MirrorCS", {"start": v(29.87, -90) * mm, "end": v(11.87, -108) * mm});
            skLineSegment(sketch, "E94.MirrorCS", {"start": v(-3.13, -120) * mm, "end": v(-3.13, -90) * mm, "construction": true});
            skSolve(sketch);
        }
        {
            var Q0;
            Q0 = qSketchRegion(id + "F16", true);
            extrude(context, id + "F17", {"entities" : qUnion([Q0]), "depth" : 25 * mm});
        }
    });
